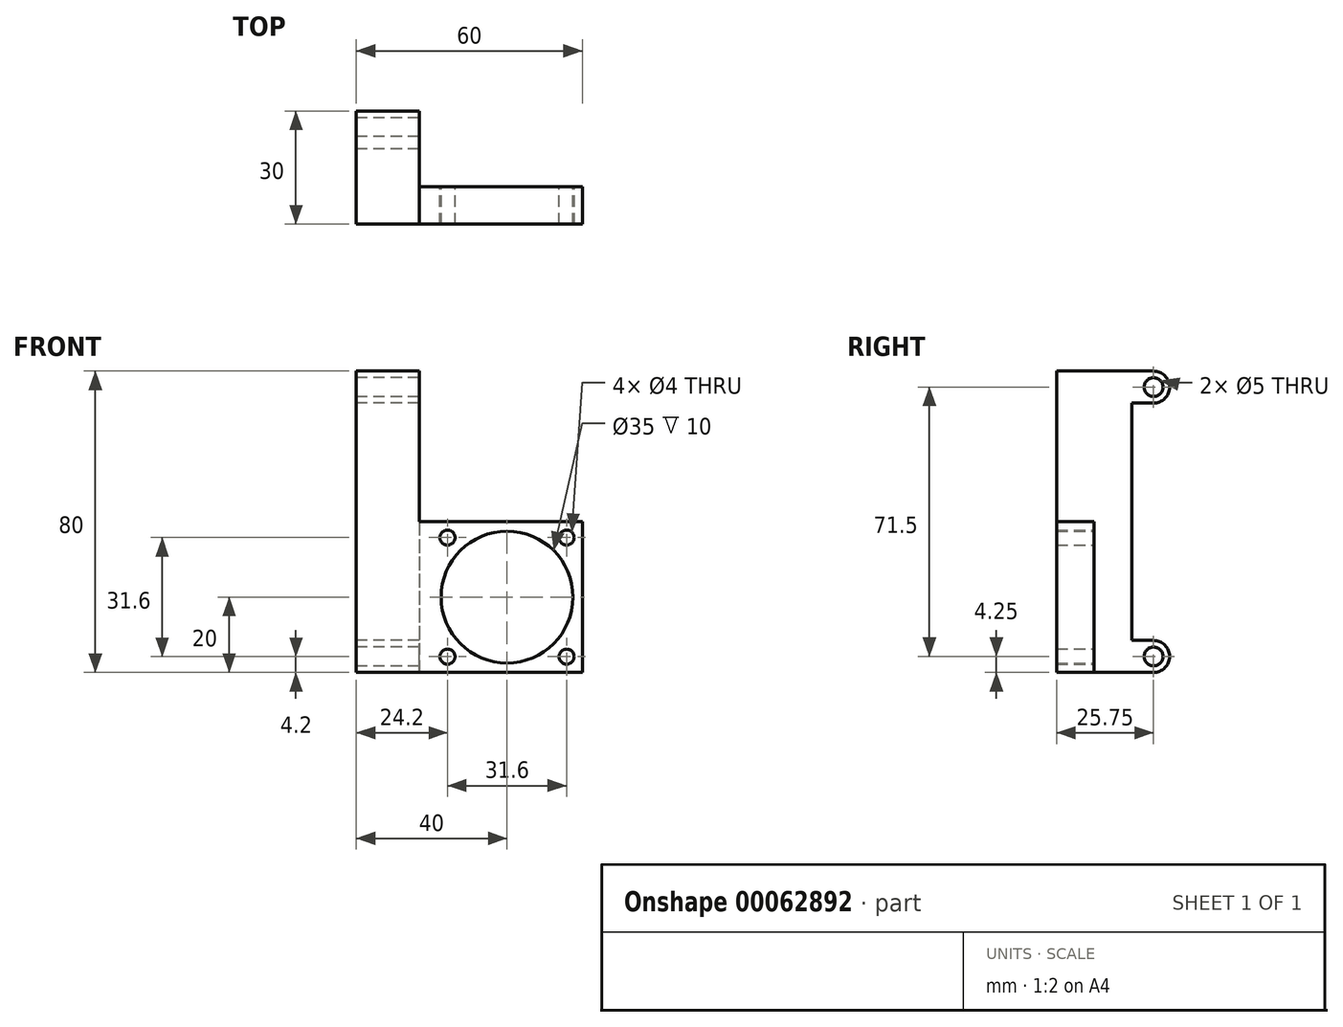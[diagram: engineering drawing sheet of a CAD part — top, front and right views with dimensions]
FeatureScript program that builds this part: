
annotation { "Feature Type Name" : "Feature", "Feature Type Description" : "" }
export const myFeature = defineFeature(function(context is Context, id is Id, definition is map)
    precondition{}
    {
        {
            var Q0;
            Q0=qCreatedBy(makeId("Top.planeOp"),FACE);
            var sketch = newSketch(context, id + "F0", { "sketchPlane" : qUnion([Q0])});
            skLineSegment(sketch, "E0.bottom", {"start": v(-40, 30) * mm, "end": v(-23.3, 30) * mm});
            skLineSegment(sketch, "E0.top", {"start": v(-40, 10) * mm, "end": v(-23.3, 10) * mm});
            skLineSegment(sketch, "E0.left", {"start": v(-40, 30) * mm, "end": v(-40, 10) * mm});
            skLineSegment(sketch, "E0.right", {"start": v(-23.3, 30) * mm, "end": v(-23.3, 10) * mm});
            skLineSegment(sketch, "E1.bottom", {"start": v(-20, 10) * mm, "end": v(20, 10) * mm});
            skLineSegment(sketch, "E1.top", {"start": v(-20, 0) * mm, "end": v(20, 0) * mm});
            skLineSegment(sketch, "E1.left", {"start": v(-20, 10) * mm, "end": v(-20, 0) * mm});
            skLineSegment(sketch, "E1.right", {"start": v(20, 10) * mm, "end": v(20, 0) * mm});
            skLineSegment(sketch, "E2.bottom", {"start": v(-20, 0) * mm, "end": v(-40, 0) * mm});
            skLineSegment(sketch, "E2.top", {"start": v(-20, 10) * mm, "end": v(-40, 10) * mm});
            skLineSegment(sketch, "E2.left", {"start": v(-20, 0) * mm, "end": v(-20, 10) * mm});
            skLineSegment(sketch, "E2.right", {"start": v(-40, 0) * mm, "end": v(-40, 10) * mm});
            skLineSegment(sketch, "E3", {"start": v(-15.8, 10) * mm, "end": v(-15.8, 5) * mm});
            skLineSegment(sketch, "E4", {"start": v(15.8, 10) * mm, "end": v(15.8, 5) * mm});
            skSolve(sketch);
        }
        {
            var Q0;
            Q0=makeQuery(id+"F0.imprint","IMPRINT",FACE,{"disambiguationData":[TD([[makeQuery(id+"F0.imprint","IMPRINT",EDGE,{"derivedFrom":sQuery(id+"F0.wireOp",EDGE,"E1.top")}),1.0]])]});
            var Q1;
            Q1=makeQuery(id+"F0.imprint","IMPRINT",FACE,{"disambiguationData":[TD([[makeQuery(id+"F0.imprint","IMPRINT",EDGE,{"derivedFrom":sQuery(id+"F0.wireOp",EDGE,"E2.bottom")}),-1.0]])]});
            extrude(context, id + "F1", {"entities" : qUnion([Q0, Q1]), "depth" : 40 * mm});
        }
        {
            var Q0;
            Q0=makeQuery(id+"F0.imprint","IMPRINT",FACE,{"disambiguationData":[TD([[makeQuery(id+"F0.imprint","IMPRINT",EDGE,{"derivedFrom":sQuery(id+"F0.wireOp",EDGE,"E0.bottom")}),-1.0]])]});
            extrude(context, id + "F2", {"entities" : qUnion([Q0]), "operationType" : NewBodyOperationType.ADD, "depth" : 80 * mm});
        }
        {
            var Q0;
            Q0=makeQuery(id+"F1.opExtrude","SWEPT_FACE",FACE,{"disambiguationData":[OSD([sQuery(id+"F0.wireOp",EDGE,"E1.bottom"),sQuery(id+"F0.wireOp",EDGE,"E2.top")])]});
            var sketch = newSketch(context, id + "F3", { "sketchPlane" : qUnion([Q0])});
            skCircle(sketch, "E5", {"center": v(-15.8, 4.2) * mm, "radius": 2 * mm});
            skCircle(sketch, "E6", {"center": v(-15.8, 35.8) * mm, "radius": 2 * mm});
            skCircle(sketch, "E7", {"center": v(15.8, 35.8) * mm, "radius": 2 * mm});
            skCircle(sketch, "E8", {"center": v(15.8, 4.2) * mm, "radius": 2 * mm});
            skCircle(sketch, "E9", {"center": v(0, 20) * mm, "radius": 17.5 * mm});
            skPoint(sketch, "E9.centerSnap0", {"position": v(-20, 20) * mm});
            skSolve(sketch);
        }
        {
            var Q0;
            Q0 = qSketchRegion(id + "F3", true);
            extrude(context, id + "F4", {"entities" : qUnion([Q0]), "operationType" : NewBodyOperationType.REMOVE, "endBound" : BoundingType.THROUGH_ALL, "oppositeDirection" : true, "depth" : 25 * mm});
        }
        {
            var Q0;
            Q0=makeQuery(id+"F2.boolean.opBoolean","MERGE",FACE,{"derivedFrom":[makeQuery(id+"F1.opExtrude","SWEPT_FACE",FACE,{"disambiguationData":[OSD([sQuery(id+"F0.wireOp",EDGE,"E2.right")])]}),makeQuery(id+"F2.opExtrude","SWEPT_FACE",FACE,{"disambiguationData":[OSD([sQuery(id+"F0.wireOp",EDGE,"E0.left")])]})]});
            var sketch = newSketch(context, id + "F5", { "sketchPlane" : qUnion([Q0])});
            skCircle(sketch, "E10", {"center": v(-25.75, 4.25) * mm, "radius": 2.5 * mm});
            skCircle(sketch, "E11", {"center": v(-25.75, 75.75) * mm, "radius": 2.5 * mm});
            skLineSegment(sketch, "E12", {"start": v(-20, 80) * mm, "end": v(-20, 0) * mm, "construction": true});
            skCircle(sketch, "E13", {"center": v(-25.75, 75.75) * mm, "radius": 4.25 * mm});
            skLineSegment(sketch, "E14", {"start": v(-25.75, 71.5) * mm, "end": v(-20, 71.5) * mm});
            skCircle(sketch, "E15", {"center": v(-25.75, 4.25) * mm, "radius": 4.25 * mm});
            skLineSegment(sketch, "E16", {"start": v(-25.75, 8.5) * mm, "end": v(-20, 8.5) * mm});
            skLineSegment(sketch, "E17", {"start": v(-20, 8.5) * mm, "end": v(-20, 71.5) * mm});
            skSolve(sketch);
        }
        {
            var Q0;
            Q0=makeQuery(id+"F5.imprint","IMPRINT",FACE,{"disambiguationData":[TD([[makeQuery(id+"F5.imprint","IMPRINT",EDGE,{"derivedFrom":sQuery(id+"F5.wireOp",EDGE,"E11")}),1.0]])]});
            var Q1;
            {var subQ0=sQuery(id+"F5.wireOp",EDGE,"E13");var subQ1=sQuery(id+"F0.wireOp",EDGE,"E0.left");var subQ4=makeQuery(id+"F2.opExtrude","CAP_EDGE",EDGE,{"disambiguationData":[OSD([subQ1])],"isStart":false});var subQ5=makeQuery(id+"F5.imprint","INTERSECT",VERTEX,{"derivedFrom":[subQ4,subQ0]});Q1=makeQuery(id+"F5.imprint","IMPRINT",FACE,{"disambiguationData":[TD([[makeQuery(id+"F5.imprint","IMPRINT",EDGE,{"disambiguationData":[TD([[subQ5,-1.0]])],"derivedFrom":subQ0}),-1.0]])]});}
            var Q2;
            {var subQ6=sQuery(id+"F5.wireOp",EDGE,"E14");Q2=makeQuery(id+"F5.imprint","IMPRINT",FACE,{"disambiguationData":[TD([[makeQuery(id+"F5.imprint","IMPRINT",EDGE,{"derivedFrom":subQ6}),-1.0]])]});}
            var Q3;
            {var subQ0=sQuery(id+"F5.wireOp",EDGE,"E15");var subQ1=sQuery(id+"F0.wireOp",EDGE,"E0.left");var subQ2=makeQuery(id+"F2.opExtrude","SWEPT_EDGE",EDGE,{"disambiguationData":[OSD([sQuery(id+"F0.wireOp",EDGE,"E0.bottom"),subQ1])]});var subQ3=makeQuery(id+"F5.imprint","INTERSECT",VERTEX,{"derivedFrom":[subQ2,subQ0]});Q3=makeQuery(id+"F5.imprint","IMPRINT",FACE,{"disambiguationData":[TD([[makeQuery(id+"F5.imprint","IMPRINT",EDGE,{"disambiguationData":[TD([[subQ3,-1.0]])],"derivedFrom":subQ0}),-1.0]])]});}
            var Q4;
            Q4=makeQuery(id+"F5.imprint","IMPRINT",FACE,{"disambiguationData":[TD([[makeQuery(id+"F5.imprint","IMPRINT",EDGE,{"derivedFrom":sQuery(id+"F5.wireOp",EDGE,"E10")}),1.0]])]});
            extrude(context, id + "F6", {"entities" : qUnion([Q0, Q1, Q2, Q3, Q4]), "operationType" : NewBodyOperationType.REMOVE, "endBound" : BoundingType.THROUGH_ALL, "oppositeDirection" : true, "depth" : 25 * mm});
        }
        {
            var Q0;
            Q0=makeQuery(id+"F1.opExtrude","CAP_FACE",FACE,{"disambiguationData":[OSD([sQuery(id+"F0.wireOp",EDGE,"E1.bottom"),sQuery(id+"F0.wireOp",EDGE,"E1.top"),sQuery(id+"F0.wireOp",EDGE,"E1.right"),sQuery(id+"F0.wireOp",EDGE,"E2.bottom"),sQuery(id+"F0.wireOp",EDGE,"E2.top"),sQuery(id+"F0.wireOp",EDGE,"E2.right")])],"isStart":false});
            var sketch = newSketch(context, id + "F7", { "sketchPlane" : qUnion([Q0])});
            skLineSegment(sketch, "E18.bottom", {"start": v(-23.3, 10) * mm, "end": v(-40, 10) * mm});
            skLineSegment(sketch, "E18.top", {"start": v(-23.3, 0) * mm, "end": v(-40, 0) * mm});
            skLineSegment(sketch, "E18.left", {"start": v(-23.3, 10) * mm, "end": v(-23.3, 0) * mm});
            skLineSegment(sketch, "E18.right", {"start": v(-40, 10) * mm, "end": v(-40, 0) * mm});
            skSolve(sketch);
        }
        {
            var Q0;
            Q0=makeQuery(id+"F7.imprint","IMPRINT",FACE,{"disambiguationData":[TD([[makeQuery(id+"F7.imprint","IMPRINT",EDGE,{"derivedFrom":sQuery(id+"F7.wireOp",EDGE,"E18.bottom")}),-1.0]])]});
            var Q1;
            Q1=makeQuery(id+"F2.opExtrude","CAP_FACE",FACE,{"disambiguationData":[OSD([sQuery(id+"F0.wireOp",EDGE,"E0.bottom"),sQuery(id+"F0.wireOp",EDGE,"E0.left"),sQuery(id+"F0.wireOp",EDGE,"E0.right"),sQuery(id+"F0.wireOp",EDGE,"E2.top")])],"isStart":false});
            extrude(context, id + "F8", {"entities" : qUnion([Q0]), "operationType" : NewBodyOperationType.ADD, "endBound" : BoundingType.UP_TO_SURFACE, "endBoundEntityFace" : qUnion([Q1]), "depth" : 25 * mm});
        }
    });
